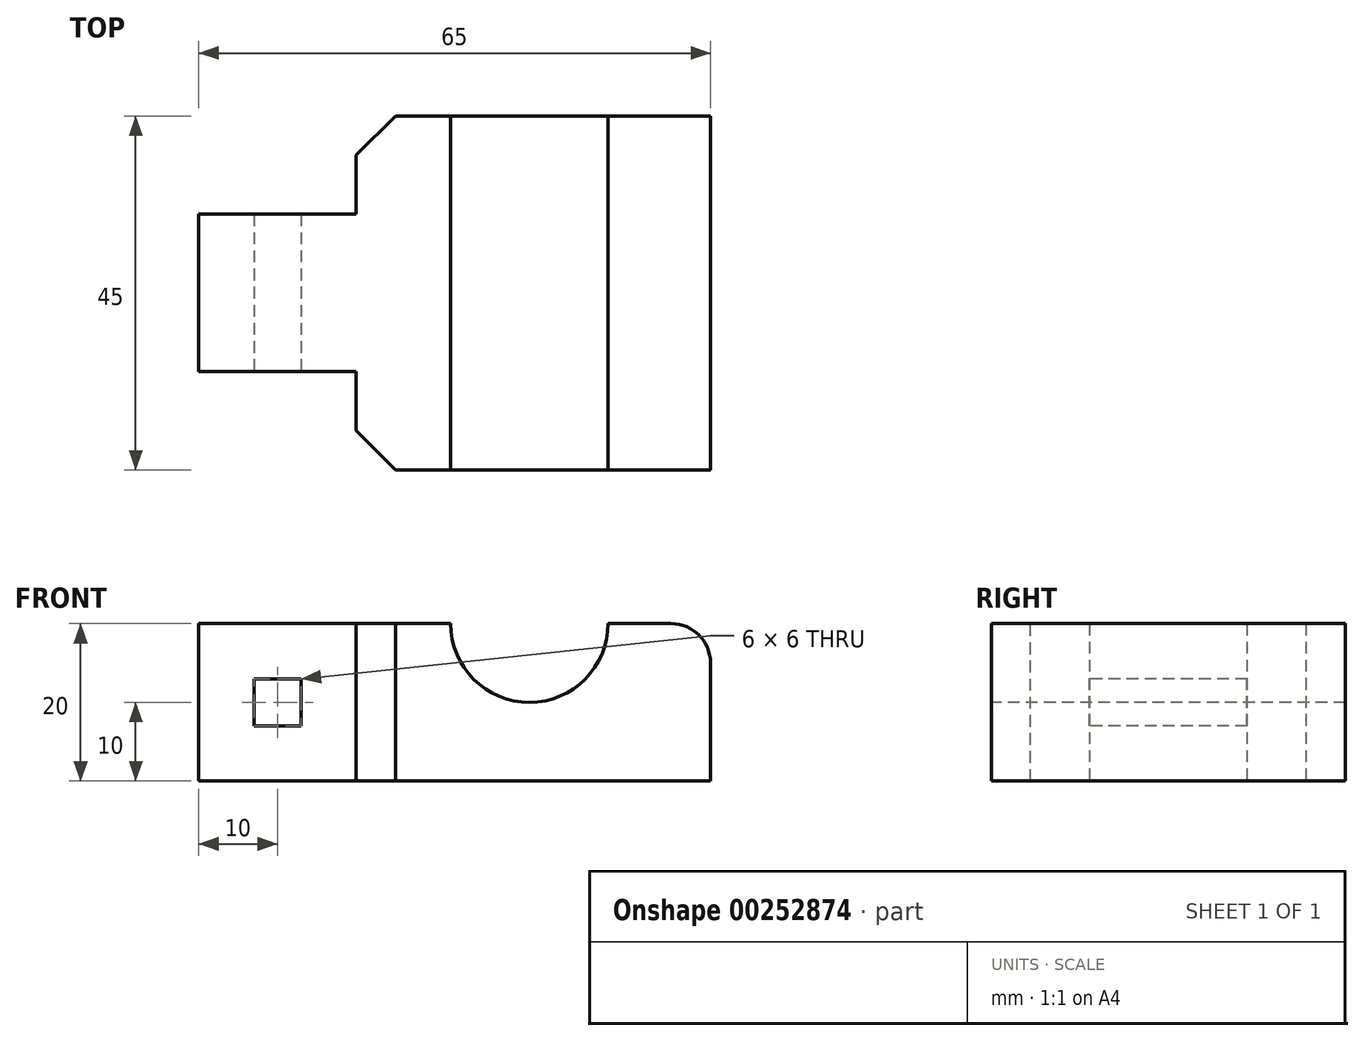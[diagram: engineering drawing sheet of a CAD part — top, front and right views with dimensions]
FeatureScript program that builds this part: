
annotation { "Feature Type Name" : "Feature", "Feature Type Description" : "" }
export const myFeature = defineFeature(function(context is Context, id is Id, definition is map)
    precondition{}
    {
        {
            var Q0;
            Q0=qCreatedBy(makeId("Top.planeOp"),FACE);
            var sketch = newSketch(context, id + "F0", { "sketchPlane" : qUnion([Q0])});
            skLineSegment(sketch, "E0.bottom", {"start": v(22.5, -22.5) * mm, "end": v(-22.5, -22.5) * mm});
            skLineSegment(sketch, "E0.top", {"start": v(22.5, 22.5) * mm, "end": v(-22.5, 22.5) * mm});
            skLineSegment(sketch, "E0.left", {"start": v(22.5, -22.5) * mm, "end": v(22.5, 22.5) * mm});
            skLineSegment(sketch, "E0.right", {"start": v(-22.5, -22.5) * mm, "end": v(-22.5, -10) * mm});
            skPoint(sketch, "E0.middle", {"position": v(0, 0) * mm});
            skLineSegment(sketch, "E1.bottom", {"start": v(-22.5, -10) * mm, "end": v(-42.5, -10) * mm});
            skLineSegment(sketch, "E1.top", {"start": v(-22.5, 10) * mm, "end": v(-42.5, 10) * mm});
            skLineSegment(sketch, "E1.right", {"start": v(-42.5, -10) * mm, "end": v(-42.5, 10) * mm});
            skPoint(sketch, "E1.middle", {"position": v(-22.5, 0) * mm});
            skPoint(sketch, "E1.left.end.orphan", {"position": v(-2.5, 10) * mm});
            skLineSegment(sketch, "E2.trimOffspring", {"start": v(-22.5, 10) * mm, "end": v(-22.5, 22.5) * mm});
            skPoint(sketch, "E3.orphan", {"position": v(-2.5, -10) * mm});
            skSolve(sketch);
        }
        {
            var Q0;
            Q0=makeQuery(id+"F0.imprint","IMPRINT",FACE,{"disambiguationData":[TD([[makeQuery(id+"F0.imprint","IMPRINT",EDGE,{"derivedFrom":sQuery(id+"F0.wireOp",EDGE,"E0.bottom")}),-1.0]])]});
            extrude(context, id + "F1", {"entities" : qUnion([Q0]), "depth" : 20 * mm});
        }
        {
            var Q0;
            Q0=makeQuery(id+"F1.opExtrude","SWEPT_EDGE",EDGE,{"disambiguationData":[OSD([sQuery(id+"F0.wireOp",EDGE,"E0.bottom"),sQuery(id+"F0.wireOp",EDGE,"E0.right")])]});
            var Q1;
            Q1=makeQuery(id+"F1.opExtrude","SWEPT_EDGE",EDGE,{"disambiguationData":[OSD([sQuery(id+"F0.wireOp",EDGE,"E0.top"),sQuery(id+"F0.wireOp",EDGE,"E2.trimOffspring")])]});
            chamfer(context, id + "F2", {"entities" : qUnion([Q0, Q1]), "width" : 5 * mm, "tangentPropagation" : true});
        }
        {
            var Q0;
            Q0=makeQuery(id+"F1.opExtrude","CAP_EDGE",EDGE,{"disambiguationData":[OSD([sQuery(id+"F0.wireOp",EDGE,"E0.left")])],"isStart":false});
            fillet(context, id + "F3", {"entities" : qUnion([Q0]), "radius" : 5 * mm, "tangentPropagation" : true, "allowEdgeOverflow" : false});
        }
        {
            var Q0;
            Q0=makeQuery(id+"F1.opExtrude","SWEPT_FACE",FACE,{"disambiguationData":[OSD([sQuery(id+"F0.wireOp",EDGE,"E1.bottom")])]});
            var sketch = newSketch(context, id + "F4", { "sketchPlane" : qUnion([Q0])});
            skLineSegment(sketch, "E4.bottom", {"start": v(-29.5, 7) * mm, "end": v(-35.5, 7) * mm});
            skLineSegment(sketch, "E4.top", {"start": v(-29.5, 13) * mm, "end": v(-35.5, 13) * mm});
            skLineSegment(sketch, "E4.left", {"start": v(-29.5, 7) * mm, "end": v(-29.5, 13) * mm});
            skLineSegment(sketch, "E4.right", {"start": v(-35.5, 7) * mm, "end": v(-35.5, 13) * mm});
            skPoint(sketch, "E4.middle", {"position": v(-32.5, 10) * mm});
            skPoint(sketch, "E4.middle.positionSnap0", {"position": v(-42.5, 10) * mm});
            skPoint(sketch, "E4.middle.positionSnap1", {"position": v(-32.5, 0) * mm});
            skPoint(sketch, "E4.centerSnap0", {"position": v(-42.5, 10) * mm});
            skPoint(sketch, "E4.centerSnap1", {"position": v(-32.5, 0) * mm});
            skCircle(sketch, "E5", {"center": v(-0.5, 20) * mm, "radius": 10 * mm});
            skSolve(sketch);
        }
        {
            var Q0;
            Q0=makeQuery(id+"F4.imprint","IMPRINT",FACE,{"disambiguationData":[TD([[makeQuery(id+"F4.imprint","IMPRINT",EDGE,{"derivedFrom":sQuery(id+"F4.wireOp",EDGE,"E5")}),1.0]])]});
            var Q1;
            Q1=makeQuery(id+"F4.imprint","IMPRINT",FACE,{"disambiguationData":[TD([[makeQuery(id+"F4.imprint","IMPRINT",EDGE,{"derivedFrom":sQuery(id+"F4.wireOp",EDGE,"E4.bottom")}),-1.0]])]});
            extrude(context, id + "F5", {"entities" : qUnion([Q0, Q1]), "operationType" : NewBodyOperationType.REMOVE, "oppositeDirection" : true, "depth" : 108.8 * mm, "symmetric" : true});
        }
    });
